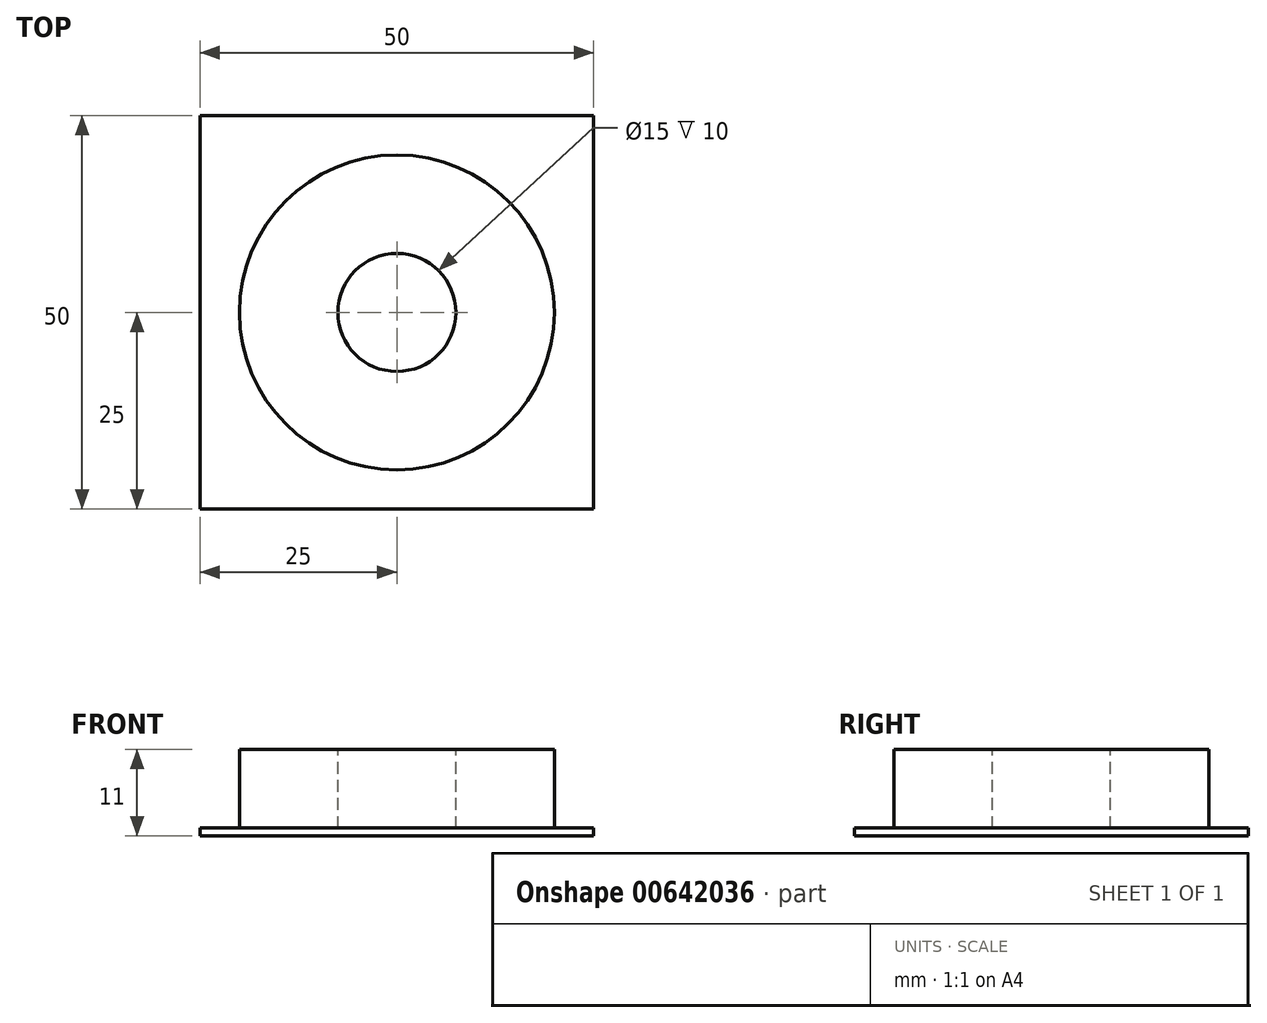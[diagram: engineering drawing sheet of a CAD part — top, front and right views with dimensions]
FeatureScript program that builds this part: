
annotation { "Feature Type Name" : "Feature", "Feature Type Description" : "" }
export const myFeature = defineFeature(function(context is Context, id is Id, definition is map)
    precondition{}
    {
        {
            var Q0;
            Q0=qCreatedBy(makeId("Top.planeOp"),FACE);
            var sketch = newSketch(context, id + "F0", { "sketchPlane" : qUnion([Q0])});
            skLineSegment(sketch, "E0.bottom", {"start": v(-25, 25) * mm, "end": v(25, 25) * mm});
            skLineSegment(sketch, "E0.top", {"start": v(-25, -25) * mm, "end": v(25, -25) * mm});
            skLineSegment(sketch, "E0.left", {"start": v(-25, 25) * mm, "end": v(-25, -25) * mm});
            skLineSegment(sketch, "E0.right", {"start": v(25, 25) * mm, "end": v(25, -25) * mm});
            skPoint(sketch, "E0.middle", {"position": v(0, 0) * mm});
            skSolve(sketch);
        }
        {
            var Q0;
            Q0=makeQuery(id+"F0.imprint","IMPRINT",FACE,{"disambiguationData":[TD([[makeQuery(id+"F0.imprint","IMPRINT",EDGE,{"derivedFrom":sQuery(id+"F0.wireOp",EDGE,"E0.bottom")}),-1.0]])]});
            extrude(context, id + "F1", {"entities" : qUnion([Q0]), "depth" : 1 * mm, "offsetDistance" : 25 * mm});
        }
        {
            var Q0;
            Q0=makeQuery(id+"F1.opExtrude","CAP_FACE",FACE,{"disambiguationData":[OSD([sQuery(id+"F0.wireOp",EDGE,"E0.bottom"),sQuery(id+"F0.wireOp",EDGE,"E0.top"),sQuery(id+"F0.wireOp",EDGE,"E0.left"),sQuery(id+"F0.wireOp",EDGE,"E0.right")])],"isStart":false});
            var sketch = newSketch(context, id + "F2", { "sketchPlane" : qUnion([Q0])});
            skCircle(sketch, "E1", {"center": v(0, 0) * mm, "radius": 20 * mm});
            skSolve(sketch);
        }
        {
            var Q0;
            Q0=makeQuery(id+"F2.imprint","IMPRINT",FACE,{"disambiguationData":[TD([[makeQuery(id+"F2.imprint","IMPRINT",EDGE,{"derivedFrom":sQuery(id+"F2.wireOp",EDGE,"E1")}),1.0]])]});
            extrude(context, id + "F3", {"entities" : qUnion([Q0]), "operationType" : NewBodyOperationType.ADD, "depth" : 10 * mm, "offsetDistance" : 25 * mm});
        }
        {
            var Q0;
            Q0=makeQuery(id+"F3.opExtrude","CAP_FACE",FACE,{"disambiguationData":[OSD([sQuery(id+"F2.wireOp",EDGE,"E1")])],"isStart":false});
            var sketch = newSketch(context, id + "F4", { "sketchPlane" : qUnion([Q0])});
            skCircle(sketch, "E2", {"center": v(0, 0) * mm, "radius": 7.5 * mm});
            skSolve(sketch);
        }
        {
            var Q0;
            Q0=makeQuery(id+"F4.imprint","IMPRINT",FACE,{"disambiguationData":[TD([[makeQuery(id+"F4.imprint","IMPRINT",EDGE,{"derivedFrom":sQuery(id+"F4.wireOp",EDGE,"E2")}),1.0]])]});
            extrude(context, id + "F5", {"entities" : qUnion([Q0]), "operationType" : NewBodyOperationType.REMOVE, "oppositeDirection" : true, "depth" : 10 * mm, "offsetDistance" : 25 * mm});
        }
    });
